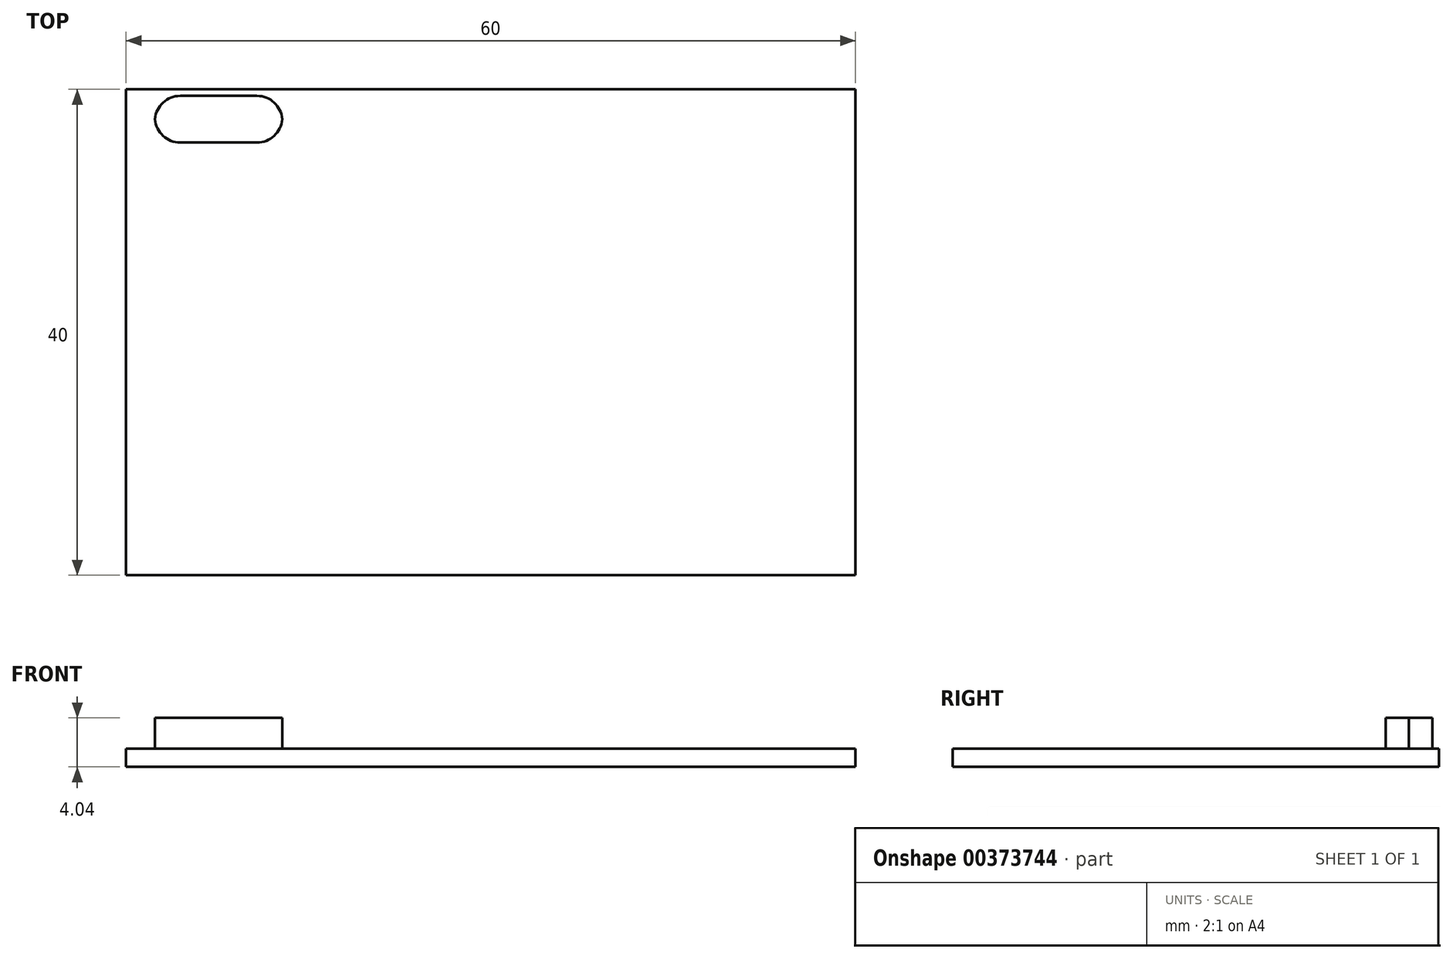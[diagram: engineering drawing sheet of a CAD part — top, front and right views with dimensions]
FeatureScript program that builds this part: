
annotation { "Feature Type Name" : "Feature", "Feature Type Description" : "" }
export const myFeature = defineFeature(function(context is Context, id is Id, definition is map)
    precondition{}
    {
        {
            var Q0;
            Q0=qCreatedBy(makeId("Front.planeOp"),FACE);
            var sketch = newSketch(context, id + "F0", { "sketchPlane" : qUnion([Q0])});
            skLineSegment(sketch, "E0.bottom", {"start": v(30, 0.75) * mm, "end": v(-30, 0.75) * mm});
            skLineSegment(sketch, "E0.top", {"start": v(30, -0.75) * mm, "end": v(-30, -0.75) * mm});
            skLineSegment(sketch, "E0.left", {"start": v(30, 0.75) * mm, "end": v(30, -0.75) * mm});
            skLineSegment(sketch, "E0.right", {"start": v(-30, 0.75) * mm, "end": v(-30, -0.75) * mm});
            skPoint(sketch, "E0.middle", {"position": v(0, 0) * mm});
            skSolve(sketch);
        }
        {
            var Q0;
            Q0 = qSketchRegion(id + "F0", true);
            extrude(context, id + "F1", {"entities" : qUnion([Q0]), "endBound" : BoundingType.SYMMETRIC, "depth" : 40 * mm});
        }
        {
            var Q0;
            Q0=makeQuery(id+"F1.opExtrude","SWEPT_FACE",FACE,{"disambiguationData":[OSD([sQuery(id+"F0.wireOp",EDGE,"E0.bottom")])]});
            var sketch = newSketch(context, id + "F2", { "sketchPlane" : qUnion([Q0])});
            skLineSegment(sketch, "E1.bottom", {"start": v(-27.63, 19.46) * mm, "end": v(-17.14, 19.46) * mm});
            skLineSegment(sketch, "E1.top", {"start": v(-27.63, 15.62) * mm, "end": v(-17.14, 15.62) * mm});
            skLineSegment(sketch, "E1.left", {"start": v(-27.63, 19.46) * mm, "end": v(-27.63, 15.62) * mm});
            skLineSegment(sketch, "E1.right", {"start": v(-17.14, 19.46) * mm, "end": v(-17.14, 15.62) * mm});
            skSolve(sketch);
        }
        {
            var Q0;
            Q0=makeQuery(id+"F2.imprint","IMPRINT",FACE,{"disambiguationData":[TD([[makeQuery(id+"F2.imprint","IMPRINT",EDGE,{"derivedFrom":sQuery(id+"F2.wireOp",EDGE,"E1.bottom")}),-1.0]])]});
            extrude(context, id + "F3", {"entities" : qUnion([Q0]), "operationType" : NewBodyOperationType.ADD, "depth" : 2.54 * mm});
        }
        {
            var Q0;
            Q0=makeQuery(id+"F3.opExtrude","SWEPT_EDGE",EDGE,{"disambiguationData":[OSD([sQuery(id+"F2.wireOp",EDGE,"E1.top"),sQuery(id+"F2.wireOp",EDGE,"E1.left")])]});
            var Q1;
            Q1=makeQuery(id+"F3.opExtrude","SWEPT_EDGE",EDGE,{"disambiguationData":[OSD([sQuery(id+"F2.wireOp",EDGE,"E1.bottom"),sQuery(id+"F2.wireOp",EDGE,"E1.left")])]});
            var Q2;
            Q2=makeQuery(id+"F3.opExtrude","SWEPT_EDGE",EDGE,{"disambiguationData":[OSD([sQuery(id+"F2.wireOp",EDGE,"E1.top"),sQuery(id+"F2.wireOp",EDGE,"E1.right")])]});
            var Q3;
            Q3=makeQuery(id+"F3.opExtrude","SWEPT_EDGE",EDGE,{"disambiguationData":[OSD([sQuery(id+"F2.wireOp",EDGE,"E1.bottom"),sQuery(id+"F2.wireOp",EDGE,"E1.right")])]});
            fillet(context, id + "F4", {"entities" : qUnion([Q0, Q1, Q2, Q3]), "radius" : 2.08 * mm, "tangentPropagation" : true, "allowEdgeOverflow" : false});
        }
    });
